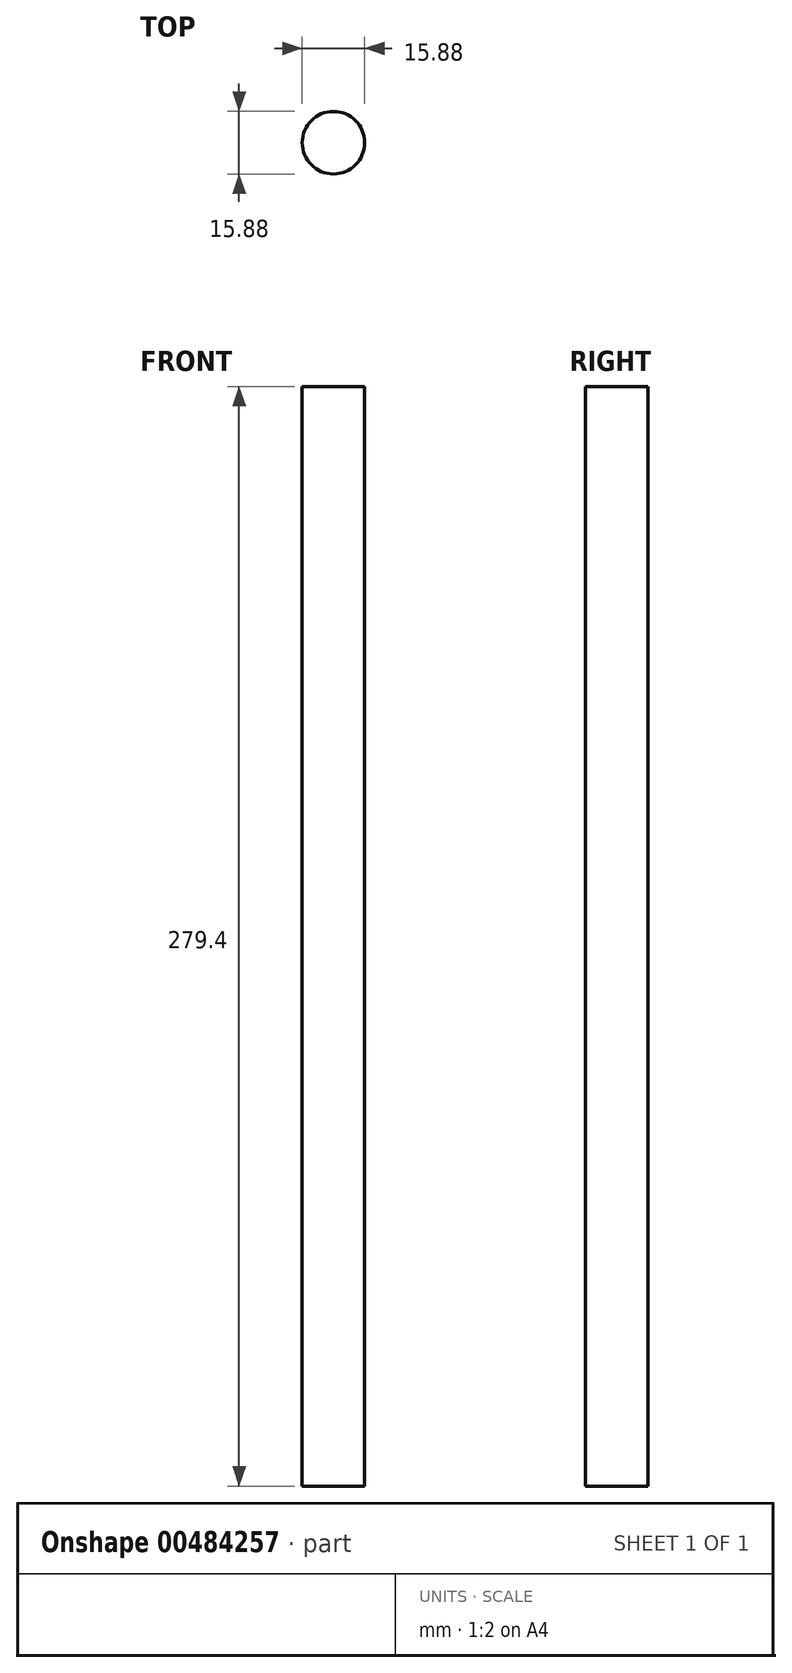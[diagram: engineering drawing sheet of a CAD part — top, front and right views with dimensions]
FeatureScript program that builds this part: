
annotation { "Feature Type Name" : "Feature", "Feature Type Description" : "" }
export const myFeature = defineFeature(function(context is Context, id is Id, definition is map)
    precondition{}
    {
        {
            var Q0;
            Q0=qCreatedBy(makeId("Top.planeOp"),FACE);
            var sketch = newSketch(context, id + "F0", { "sketchPlane" : qUnion([Q0])});
            skCircle(sketch, "E0", {"center": v(0, 0) * mm, "radius": 7.94 * mm});
            skSolve(sketch);
        }
        {
            var Q0;
            Q0=makeQuery(id+"F0.imprint","IMPRINT",FACE,{"disambiguationData":[TD([[makeQuery(id+"F0.imprint","IMPRINT",EDGE,{"derivedFrom":sQuery(id+"F0.wireOp",EDGE,"E0")}),1.0]])]});
            extrude(context, id + "F1", {"entities" : qUnion([Q0]), "depth" : 279.4 * mm});
        }
    });
